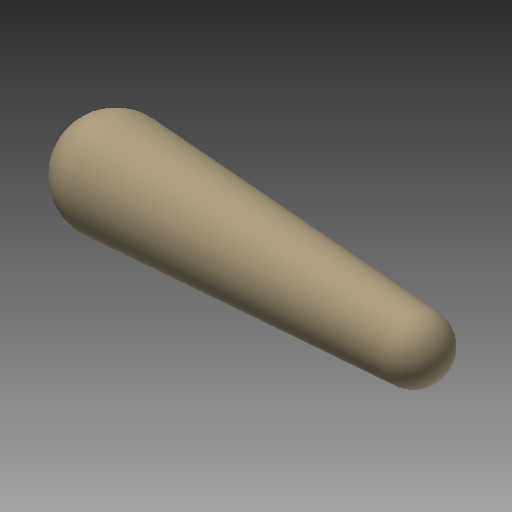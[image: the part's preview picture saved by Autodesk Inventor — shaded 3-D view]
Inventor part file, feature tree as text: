
AUTODESK INVENTOR PART (.ipt)
format: ipt  version: 2022 (Build 260153000, 153)  size: 166,912 bytes
history: native  units: mm (DEFAULTED — no unit token found)
features: other x1, revolve x1, sketch x1
ambient origin geometry x8: Origin, YZ Plane, XZ Plane, XY Plane, X Axis, Y Axis, Z Axis, Center Point
bodies: Solid1 (feature_tree)
feature tree (3):
  other  "iMandy - 2D BODY"
  revolve  "Revolution1"  [1 undecoded]
  sketch  "Sketch1"  dims[d1=10.0mm d16=234.95mm d17=75.692mm d18=48.006mm d19=90.0deg]
note: 1 required parameter value undecoded (feature->parameter linkage not recoverable at this tier; creation-order binding heuristic only, values carry confidence <= 0.55)
